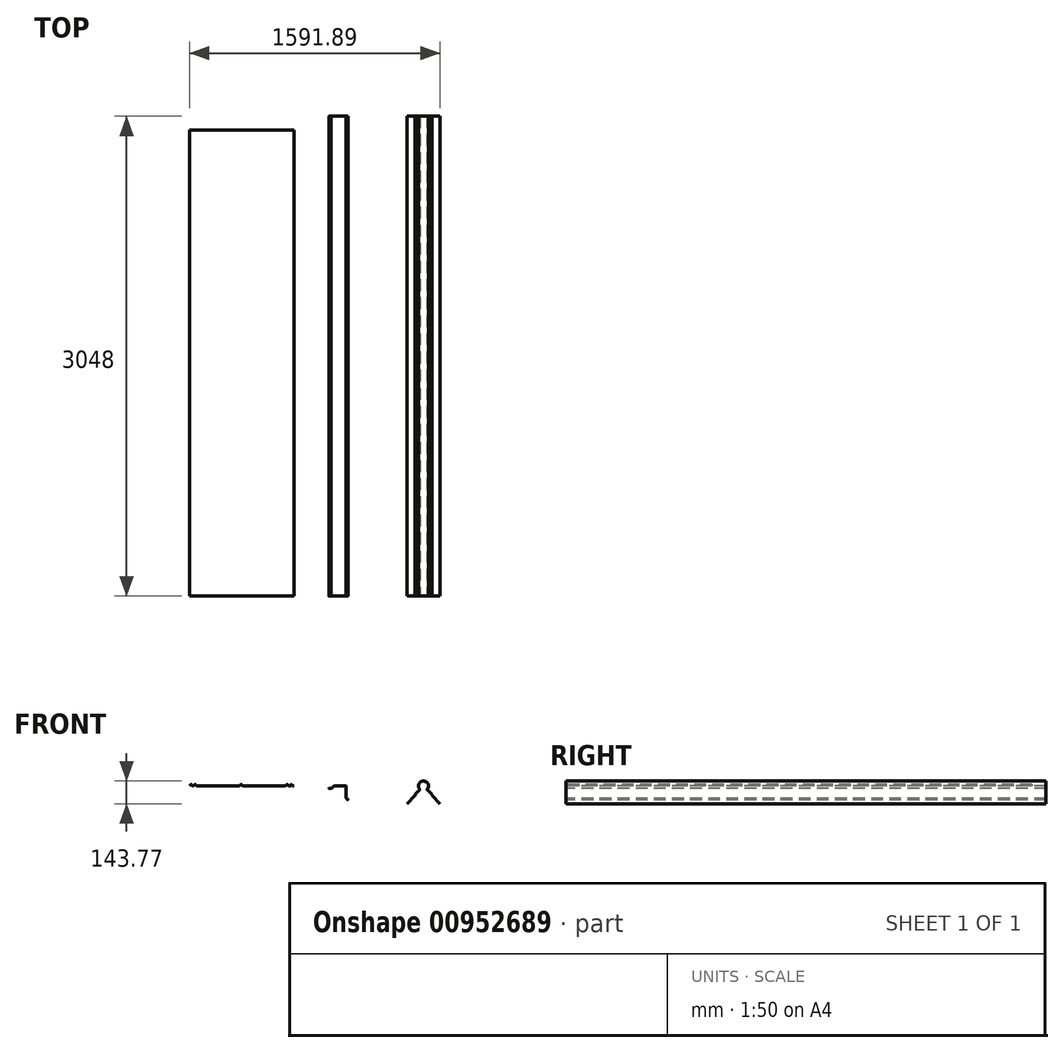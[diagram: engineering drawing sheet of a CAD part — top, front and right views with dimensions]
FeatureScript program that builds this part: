
annotation { "Feature Type Name" : "Feature", "Feature Type Description" : "" }
export const myFeature = defineFeature(function(context is Context, id is Id, definition is map)
    precondition{}
    {
        {
            var Q0;
            Q0=qCreatedBy(makeId("Front.planeOp"),FACE);
            var sketch = newSketch(context, id + "F0", { "sketchPlane" : qUnion([Q0])});
            skLineSegment(sketch, "E0.top", {"start": v(-1486.48, 424.6) * mm, "end": v(-822.9, 424.6) * mm, "construction": true});
            skLineSegment(sketch, "E0.left", {"start": v(-1486.48, 413.38) * mm, "end": v(-1486.48, 424.6) * mm, "construction": true});
            skLineSegment(sketch, "E0.right", {"start": v(-822.9, 413.38) * mm, "end": v(-822.9, 424.6) * mm, "construction": true});
            skLineSegment(sketch, "E1", {"start": v(-1485.6, 413.82) * mm, "end": v(-1475.55, 424.4) * mm});
            skLineSegment(sketch, "E2", {"start": v(-1475.55, 423.88) * mm, "end": v(-1485.44, 413.46) * mm});
            skLineSegment(sketch, "E3", {"start": v(-1475.18, 423.88) * mm, "end": v(-1465.29, 413.46) * mm});
            skLineSegment(sketch, "E4", {"start": v(-1475.18, 424.4) * mm, "end": v(-1465.14, 413.82) * mm});
            skPoint(sketch, "E5.visualSharp", {"position": v(-1475.37, 424.6) * mm});
            skArc(sketch, "E5.filletArc", {"start": v(-1475.18, 424.4) * mm, "mid": v(-1475.37, 424.48) * mm, "end": v(-1475.55, 424.4) * mm});
            skPoint(sketch, "E6.visualSharp", {"position": v(-1475.37, 424.08) * mm});
            skArc(sketch, "E6.filletArc", {"start": v(-1475.18, 423.88) * mm, "mid": v(-1475.37, 423.96) * mm, "end": v(-1475.55, 423.88) * mm});
            skPoint(sketch, "E7", {"position": v(-1475.37, 424.48) * mm});
            skPoint(sketch, "E8", {"position": v(-1465.21, 413.38) * mm});
            skPoint(sketch, "E9", {"position": v(-1485.52, 413.38) * mm});
            skPoint(sketch, "E10", {"position": v(-1465.06, 413.74) * mm});
            skPoint(sketch, "E11.1.0.0", {"position": v(-1449.97, 424.6) * mm});
            skPoint(sketch, "E11.1.0.1", {"position": v(-1449.97, 424.08) * mm});
            skPoint(sketch, "E11.1.0.2", {"position": v(-1460.27, 413.74) * mm});
            skPoint(sketch, "E11.1.0.3", {"position": v(-1460.12, 413.38) * mm});
            skPoint(sketch, "E11.1.0.4", {"position": v(-1439.66, 413.74) * mm});
            skPoint(sketch, "E11.1.0.5", {"position": v(-1439.81, 413.38) * mm});
            skPoint(sketch, "E12.1.0.0", {"position": v(-1157.87, 424.6) * mm});
            skPoint(sketch, "E12.1.0.1", {"position": v(-1157.87, 424.08) * mm});
            skPoint(sketch, "E12.1.0.2", {"position": v(-1168.17, 413.74) * mm});
            skPoint(sketch, "E12.1.0.3", {"position": v(-1168.02, 413.38) * mm});
            skPoint(sketch, "E12.1.0.4", {"position": v(-1147.71, 413.38) * mm});
            skPoint(sketch, "E12.1.0.5", {"position": v(-1147.56, 413.74) * mm});
            skPoint(sketch, "E12.2.0.0", {"position": v(-865.77, 424.6) * mm});
            skPoint(sketch, "E12.2.0.1", {"position": v(-865.77, 424.08) * mm});
            skPoint(sketch, "E12.2.0.2", {"position": v(-876.07, 413.74) * mm});
            skPoint(sketch, "E12.2.0.3", {"position": v(-875.92, 413.38) * mm});
            skPoint(sketch, "E12.2.0.4", {"position": v(-855.61, 413.38) * mm});
            skPoint(sketch, "E12.2.0.5", {"position": v(-855.46, 413.74) * mm});
            skLineSegment(sketch, "E12.direction1", {"start": v(-1449.97, 424.6) * mm, "end": v(-1157.87, 424.6) * mm, "construction": true});
            skPoint(sketch, "E13.1.0.0", {"position": v(-840.37, 424.6) * mm});
            skPoint(sketch, "E13.1.0.1", {"position": v(-830.06, 413.74) * mm});
            skPoint(sketch, "E13.1.0.2", {"position": v(-830.21, 413.38) * mm});
            skPoint(sketch, "E13.1.0.3", {"position": v(-840.26, 423.96) * mm});
            skLineSegment(sketch, "E13.direction1", {"start": v(-865.77, 424.6) * mm, "end": v(-840.37, 424.6) * mm, "construction": true});
            skPoint(sketch, "E14", {"position": v(-845.13, 413.74) * mm});
            skLineSegment(sketch, "E15", {"start": v(-1460.2, 413.82) * mm, "end": v(-1450.15, 424.4) * mm});
            skLineSegment(sketch, "E16", {"start": v(-1460.04, 413.46) * mm, "end": v(-1450.15, 423.88) * mm});
            skLineSegment(sketch, "E17", {"start": v(-1449.78, 424.4) * mm, "end": v(-1439.74, 413.82) * mm});
            skLineSegment(sketch, "E18", {"start": v(-1449.78, 423.88) * mm, "end": v(-1439.89, 413.46) * mm});
            skLineSegment(sketch, "E19", {"start": v(-1168.1, 413.82) * mm, "end": v(-1158.05, 424.4) * mm});
            skLineSegment(sketch, "E20", {"start": v(-1167.94, 413.46) * mm, "end": v(-1158.05, 423.88) * mm});
            skLineSegment(sketch, "E21", {"start": v(-1157.68, 424.4) * mm, "end": v(-1147.64, 413.82) * mm});
            skLineSegment(sketch, "E22", {"start": v(-1157.68, 423.88) * mm, "end": v(-1147.79, 413.46) * mm});
            skLineSegment(sketch, "E23", {"start": v(-876, 413.82) * mm, "end": v(-865.95, 424.4) * mm});
            skLineSegment(sketch, "E24", {"start": v(-865.58, 424.4) * mm, "end": v(-855.54, 413.82) * mm});
            skLineSegment(sketch, "E25", {"start": v(-875.84, 413.46) * mm, "end": v(-865.95, 423.88) * mm});
            skLineSegment(sketch, "E26", {"start": v(-865.58, 423.88) * mm, "end": v(-855.69, 413.46) * mm});
            skLineSegment(sketch, "E27", {"start": v(-845.06, 413.89) * mm, "end": v(-840.52, 424.25) * mm});
            skLineSegment(sketch, "E28", {"start": v(-840.4, 423.61) * mm, "end": v(-844.83, 413.53) * mm});
            skLineSegment(sketch, "E29", {"start": v(-840.1, 424.32) * mm, "end": v(-830.14, 413.82) * mm});
            skLineSegment(sketch, "E30", {"start": v(-840, 423.68) * mm, "end": v(-830.29, 413.46) * mm});
            skLineSegment(sketch, "E31", {"start": v(-1486.48, 413.38) * mm, "end": v(-1486.48, 413.74) * mm});
            skLineSegment(sketch, "E32", {"start": v(-1486.48, 413.74) * mm, "end": v(-1485.78, 413.74) * mm});
            skLineSegment(sketch, "E33", {"start": v(-1486.48, 413.38) * mm, "end": v(-1485.63, 413.38) * mm});
            skLineSegment(sketch, "E34", {"start": v(-830.1, 413.38) * mm, "end": v(-822.9, 413.38) * mm});
            skLineSegment(sketch, "E35", {"start": v(-822.9, 413.38) * mm, "end": v(-822.9, 413.74) * mm});
            skLineSegment(sketch, "E36", {"start": v(-822.9, 413.74) * mm, "end": v(-829.95, 413.74) * mm});
            skLineSegment(sketch, "E37", {"start": v(-845.3, 413.74) * mm, "end": v(-855.35, 413.74) * mm});
            skLineSegment(sketch, "E38", {"start": v(-855.5, 413.38) * mm, "end": v(-845.06, 413.38) * mm});
            skLineSegment(sketch, "E39", {"start": v(-876.18, 413.74) * mm, "end": v(-1147.45, 413.74) * mm});
            skLineSegment(sketch, "E40", {"start": v(-1147.6, 413.38) * mm, "end": v(-876.03, 413.38) * mm});
            skLineSegment(sketch, "E41", {"start": v(-1168.28, 413.74) * mm, "end": v(-1439.55, 413.74) * mm});
            skLineSegment(sketch, "E42", {"start": v(-1439.7, 413.38) * mm, "end": v(-1168.13, 413.38) * mm});
            skLineSegment(sketch, "E43", {"start": v(-1464.95, 413.74) * mm, "end": v(-1460.38, 413.74) * mm});
            skLineSegment(sketch, "E44", {"start": v(-1465.1, 413.38) * mm, "end": v(-1460.23, 413.38) * mm});
            skPoint(sketch, "E45.visualSharp", {"position": v(-1485.67, 413.74) * mm});
            skArc(sketch, "E45.filletArc", {"start": v(-1485.78, 413.74) * mm, "mid": v(-1485.68, 413.76) * mm, "end": v(-1485.6, 413.82) * mm});
            skArc(sketch, "E46.filletArc", {"start": v(-1485.63, 413.38) * mm, "mid": v(-1485.53, 413.4) * mm, "end": v(-1485.44, 413.46) * mm});
            skArc(sketch, "E47.filletArc", {"start": v(-1465.14, 413.82) * mm, "mid": v(-1465.05, 413.76) * mm, "end": v(-1464.95, 413.74) * mm});
            skArc(sketch, "E48.filletArc", {"start": v(-1465.29, 413.46) * mm, "mid": v(-1465.2, 413.4) * mm, "end": v(-1465.1, 413.38) * mm});
            skArc(sketch, "E49.filletArc", {"start": v(-1460.38, 413.74) * mm, "mid": v(-1460.28, 413.76) * mm, "end": v(-1460.2, 413.82) * mm});
            skArc(sketch, "E50.filletArc", {"start": v(-1460.23, 413.38) * mm, "mid": v(-1460.13, 413.4) * mm, "end": v(-1460.04, 413.46) * mm});
            skArc(sketch, "E51.filletArc", {"start": v(-1439.89, 413.46) * mm, "mid": v(-1439.8, 413.4) * mm, "end": v(-1439.7, 413.38) * mm});
            skArc(sketch, "E52.filletArc", {"start": v(-1439.74, 413.82) * mm, "mid": v(-1439.65, 413.76) * mm, "end": v(-1439.55, 413.74) * mm});
            skArc(sketch, "E53.filletArc", {"start": v(-1168.13, 413.38) * mm, "mid": v(-1168.03, 413.4) * mm, "end": v(-1167.94, 413.46) * mm});
            skArc(sketch, "E54.filletArc", {"start": v(-1168.28, 413.74) * mm, "mid": v(-1168.18, 413.76) * mm, "end": v(-1168.1, 413.82) * mm});
            skArc(sketch, "E55.filletArc", {"start": v(-1147.79, 413.46) * mm, "mid": v(-1147.7, 413.4) * mm, "end": v(-1147.6, 413.38) * mm});
            skArc(sketch, "E56.filletArc", {"start": v(-1147.64, 413.82) * mm, "mid": v(-1147.55, 413.76) * mm, "end": v(-1147.45, 413.74) * mm});
            skArc(sketch, "E57.filletArc", {"start": v(-876.18, 413.74) * mm, "mid": v(-876.08, 413.76) * mm, "end": v(-876, 413.82) * mm});
            skArc(sketch, "E58.filletArc", {"start": v(-876.03, 413.38) * mm, "mid": v(-875.93, 413.4) * mm, "end": v(-875.84, 413.46) * mm});
            skArc(sketch, "E59.filletArc", {"start": v(-865.58, 423.88) * mm, "mid": v(-865.77, 423.96) * mm, "end": v(-865.95, 423.88) * mm});
            skArc(sketch, "E60.filletArc", {"start": v(-865.58, 424.4) * mm, "mid": v(-865.77, 424.48) * mm, "end": v(-865.95, 424.4) * mm});
            skArc(sketch, "E61.filletArc", {"start": v(-855.54, 413.82) * mm, "mid": v(-855.45, 413.76) * mm, "end": v(-855.35, 413.74) * mm});
            skArc(sketch, "E62.filletArc", {"start": v(-855.69, 413.46) * mm, "mid": v(-855.6, 413.4) * mm, "end": v(-855.5, 413.38) * mm});
            skArc(sketch, "E63.filletArc", {"start": v(-845.3, 413.74) * mm, "mid": v(-845.16, 413.78) * mm, "end": v(-845.06, 413.89) * mm});
            skPoint(sketch, "E64.visualSharp", {"position": v(-844.9, 413.38) * mm});
            skArc(sketch, "E64.filletArc", {"start": v(-845.06, 413.38) * mm, "mid": v(-844.92, 413.42) * mm, "end": v(-844.83, 413.53) * mm});
            skArc(sketch, "E65.filletArc", {"start": v(-840.1, 424.32) * mm, "mid": v(-840.33, 424.4) * mm, "end": v(-840.52, 424.25) * mm});
            skArc(sketch, "E66.filletArc", {"start": v(-840, 423.68) * mm, "mid": v(-840.22, 423.76) * mm, "end": v(-840.4, 423.61) * mm});
            skArc(sketch, "E67.filletArc", {"start": v(-830.14, 413.82) * mm, "mid": v(-830.05, 413.76) * mm, "end": v(-829.95, 413.74) * mm});
            skArc(sketch, "E68.filletArc", {"start": v(-830.29, 413.46) * mm, "mid": v(-830.2, 413.4) * mm, "end": v(-830.1, 413.38) * mm});
            skArc(sketch, "E69.filletArc", {"start": v(-1157.68, 423.88) * mm, "mid": v(-1157.87, 423.96) * mm, "end": v(-1158.05, 423.88) * mm});
            skArc(sketch, "E70.filletArc", {"start": v(-1157.68, 424.4) * mm, "mid": v(-1157.87, 424.48) * mm, "end": v(-1158.05, 424.4) * mm});
            skArc(sketch, "E71.filletArc", {"start": v(-1449.78, 423.88) * mm, "mid": v(-1449.97, 423.96) * mm, "end": v(-1450.15, 423.88) * mm});
            skArc(sketch, "E72.filletArc", {"start": v(-1449.78, 424.4) * mm, "mid": v(-1449.97, 424.48) * mm, "end": v(-1450.15, 424.4) * mm});
            skArc(sketch, "E73", {"start": v(22.63, 391.1) * mm, "mid": v(0, 445.13) * mm, "end": v(-22.63, 391.1) * mm});
            skArc(sketch, "E74", {"start": v(22.13, 391.1) * mm, "mid": v(0, 444.77) * mm, "end": v(-22.13, 391.1) * mm});
            skLineSegment(sketch, "E75", {"start": v(0, 413.38) * mm, "end": v(0.25, 413.13) * mm});
            skLineSegment(sketch, "E76", {"start": v(0, 413.38) * mm, "end": v(0, 231.35) * mm, "construction": true});
            skCircle(sketch, "E77", {"center": v(0, 413.38) * mm, "radius": 0.36 * mm, "construction": true});
            skLineSegment(sketch, "E78", {"start": v(0.25, 413.13) * mm, "end": v(0, 412.87) * mm, "construction": true});
            skLineSegment(sketch, "E79", {"start": v(0, 412.87) * mm, "end": v(-0.25, 413.13) * mm, "construction": true});
            skLineSegment(sketch, "E80", {"start": v(22.12, 390.75) * mm, "end": v(53.45, 359.42) * mm});
            skLineSegment(sketch, "E81", {"start": v(53.52, 359.24) * mm, "end": v(53.52, 353.1) * mm});
            skLineSegment(sketch, "E82.1.0.0", {"start": v(53.88, 359.4) * mm, "end": v(53.88, 353.25) * mm});
            skLineSegment(sketch, "E83", {"start": v(53.6, 352.93) * mm, "end": v(105.16, 301.36) * mm});
            skLineSegment(sketch, "E84.trimOffspring", {"start": v(22.63, 390.75) * mm, "end": v(53.8, 359.57) * mm});
            skLineSegment(sketch, "E85", {"start": v(105.16, 301.36) * mm, "end": v(105.41, 301.62) * mm});
            skLineSegment(sketch, "E86", {"start": v(105.41, 301.62) * mm, "end": v(53.96, 353.07) * mm});
            skPoint(sketch, "E87.visualSharp", {"position": v(21.94, 390.93) * mm});
            skArc(sketch, "E87.filletArc", {"start": v(22.13, 391.1) * mm, "mid": v(22.05, 390.93) * mm, "end": v(22.12, 390.75) * mm});
            skPoint(sketch, "E88.visualSharp", {"position": v(22.45, 390.93) * mm});
            skArc(sketch, "E88.filletArc", {"start": v(22.63, 391.1) * mm, "mid": v(22.56, 390.93) * mm, "end": v(22.63, 390.75) * mm});
            skPoint(sketch, "E89.visualSharp", {"position": v(53.52, 359.35) * mm});
            skArc(sketch, "E89.filletArc", {"start": v(53.52, 359.24) * mm, "mid": v(53.5, 359.34) * mm, "end": v(53.45, 359.42) * mm});
            skPoint(sketch, "E90.visualSharp", {"position": v(53.88, 359.5) * mm});
            skArc(sketch, "E90.filletArc", {"start": v(53.88, 359.4) * mm, "mid": v(53.86, 359.5) * mm, "end": v(53.8, 359.57) * mm});
            skPoint(sketch, "E91.visualSharp", {"position": v(53.52, 353) * mm});
            skArc(sketch, "E91.filletArc", {"start": v(53.52, 353.1) * mm, "mid": v(53.54, 353) * mm, "end": v(53.6, 352.93) * mm});
            skPoint(sketch, "E92.visualSharp", {"position": v(53.88, 353.15) * mm});
            skArc(sketch, "E92.filletArc", {"start": v(53.88, 353.25) * mm, "mid": v(53.9, 353.16) * mm, "end": v(53.96, 353.07) * mm});
            skArc(sketch, "E93.MirrorCS", {"start": v(-22.13, 391.1) * mm, "mid": v(-22.05, 390.93) * mm, "end": v(-22.12, 390.75) * mm});
            skArc(sketch, "E94.MirrorCS", {"start": v(-22.63, 391.1) * mm, "mid": v(-22.56, 390.93) * mm, "end": v(-22.63, 390.75) * mm});
            skPoint(sketch, "E95.MirrorP", {"position": v(-21.94, 390.93) * mm});
            skPoint(sketch, "E96.MirrorP", {"position": v(-22.45, 390.93) * mm});
            skLineSegment(sketch, "E97.MirrorCS", {"start": v(-22.12, 390.75) * mm, "end": v(-53.45, 359.42) * mm});
            skLineSegment(sketch, "E98.MirrorCS", {"start": v(-22.63, 390.75) * mm, "end": v(-53.8, 359.57) * mm});
            skArc(sketch, "E99.MirrorCS", {"start": v(-53.52, 353.1) * mm, "mid": v(-53.54, 353) * mm, "end": v(-53.6, 352.93) * mm});
            skArc(sketch, "E100.MirrorCS", {"start": v(-53.52, 359.24) * mm, "mid": v(-53.5, 359.34) * mm, "end": v(-53.45, 359.42) * mm});
            skArc(sketch, "E101.MirrorCS", {"start": v(-53.88, 353.25) * mm, "mid": v(-53.9, 353.16) * mm, "end": v(-53.96, 353.07) * mm});
            skArc(sketch, "E102.MirrorCS", {"start": v(-53.88, 359.4) * mm, "mid": v(-53.86, 359.5) * mm, "end": v(-53.8, 359.57) * mm});
            skLineSegment(sketch, "E103.MirrorCS", {"start": v(-53.52, 359.24) * mm, "end": v(-53.52, 353.1) * mm});
            skLineSegment(sketch, "E104.MirrorCS", {"start": v(-53.88, 359.4) * mm, "end": v(-53.88, 353.25) * mm});
            skLineSegment(sketch, "E105.MirrorCS", {"start": v(-105.16, 301.36) * mm, "end": v(-105.41, 301.62) * mm});
            skPoint(sketch, "E106.MirrorP", {"position": v(-53.88, 353.15) * mm});
            skPoint(sketch, "E107.MirrorP", {"position": v(-53.52, 359.35) * mm});
            skPoint(sketch, "E108.MirrorP", {"position": v(-53.88, 359.5) * mm});
            skPoint(sketch, "E109.MirrorP", {"position": v(-53.52, 353) * mm});
            skLineSegment(sketch, "E110.MirrorCS", {"start": v(-53.6, 352.93) * mm, "end": v(-105.16, 301.36) * mm});
            skLineSegment(sketch, "E111.MirrorCS", {"start": v(-105.41, 301.62) * mm, "end": v(-53.96, 353.07) * mm});
            skLineSegment(sketch, "E112.left", {"start": v(-822.9, 413.38) * mm, "end": v(-822.9, 413.74) * mm, "construction": true});
            skLineSegment(sketch, "E113", {"start": v(-568.6, 413.74) * mm, "end": v(-491.83, 413.74) * mm});
            skLineSegment(sketch, "E114", {"start": v(-568.6, 413.38) * mm, "end": v(-491.83, 413.38) * mm});
            skLineSegment(sketch, "E115", {"start": v(-491.12, 413.02) * mm, "end": v(-491.12, 337.83) * mm});
            skLineSegment(sketch, "E116", {"start": v(-491.01, 337.58) * mm, "end": v(-480.74, 327.31) * mm});
            skLineSegment(sketch, "E117", {"start": v(-482.27, 325.9) * mm, "end": v(-489.62, 334.68) * mm});
            skLineSegment(sketch, "E118", {"start": v(-489.35, 334.9) * mm, "end": v(-482, 326.14) * mm});
            skLineSegment(sketch, "E119", {"start": v(-481, 327.06) * mm, "end": v(-491.26, 337.33) * mm});
            skLineSegment(sketch, "E120", {"start": v(-491.47, 337.83) * mm, "end": v(-491.47, 413.02) * mm});
            skPoint(sketch, "E121.visualSharp", {"position": v(-491.47, 337.54) * mm});
            skArc(sketch, "E121.filletArc", {"start": v(-491.47, 337.83) * mm, "mid": v(-491.42, 337.56) * mm, "end": v(-491.26, 337.33) * mm});
            skArc(sketch, "E122.filletArc", {"start": v(-491.12, 413.02) * mm, "mid": v(-491.33, 413.53) * mm, "end": v(-491.83, 413.74) * mm});
            skPoint(sketch, "E123.visualSharp", {"position": v(-490.97, 337.54) * mm});
            skLineSegment(sketch, "E124", {"start": v(-584.77, 397.66) * mm, "end": v(-599.27, 397.66) * mm});
            skLineSegment(sketch, "E125", {"start": v(-625.98, 383.07) * mm, "end": v(-625.98, 383.07) * mm});
            skLineSegment(sketch, "E126", {"start": v(-587.77, 398.38) * mm, "end": v(-599.2, 399.39) * mm});
            skLineSegment(sketch, "E127", {"start": v(-599.27, 398.02) * mm, "end": v(-584.77, 398.02) * mm});
            skLineSegment(sketch, "E128", {"start": v(-569.11, 413.53) * mm, "end": v(-584.51, 398.13) * mm});
            skLineSegment(sketch, "E129", {"start": v(-568.86, 413.27) * mm, "end": v(-584.26, 397.87) * mm});
            skLineSegment(sketch, "E130", {"start": v(-587.74, 398.73) * mm, "end": v(-599.18, 399.74) * mm});
            skArc(sketch, "E131", {"start": v(-599.18, 399.74) * mm, "mid": v(-600.3, 398.75) * mm, "end": v(-599.27, 397.66) * mm, "construction": true});
            skArc(sketch, "E132", {"start": v(-599.2, 399.39) * mm, "mid": v(-599.95, 398.73) * mm, "end": v(-599.27, 398.02) * mm});
            skArc(sketch, "E133", {"start": v(-599.18, 399.74) * mm, "mid": v(-600.3, 398.75) * mm, "end": v(-599.27, 397.66) * mm});
            skPoint(sketch, "E134", {"position": v(-600.3, 398.75) * mm});
            skArc(sketch, "E135", {"start": v(-587.74, 398.73) * mm, "mid": v(-587.58, 398.54) * mm, "end": v(-587.77, 398.38) * mm});
            skPoint(sketch, "E136", {"position": v(-587.58, 398.54) * mm});
            skLineSegment(sketch, "E137", {"start": v(-600.3, 398.75) * mm, "end": v(-600.23, 399.65) * mm, "construction": true});
            skLineSegment(sketch, "E138", {"start": v(-600.23, 399.65) * mm, "end": v(-587.58, 398.54) * mm, "construction": true});
            skPoint(sketch, "E139.visualSharp", {"position": v(-584.62, 398.02) * mm});
            skArc(sketch, "E139.filletArc", {"start": v(-584.77, 398.02) * mm, "mid": v(-584.63, 398.05) * mm, "end": v(-584.51, 398.13) * mm});
            skArc(sketch, "E140.filletArc", {"start": v(-568.6, 413.38) * mm, "mid": v(-568.74, 413.35) * mm, "end": v(-568.86, 413.27) * mm});
            skArc(sketch, "E141.filletArc", {"start": v(-491.47, 413.02) * mm, "mid": v(-491.58, 413.27) * mm, "end": v(-491.83, 413.38) * mm});
            skArc(sketch, "E142.filletArc", {"start": v(-491.12, 337.83) * mm, "mid": v(-491.09, 337.7) * mm, "end": v(-491.01, 337.58) * mm});
            skPoint(sketch, "E143.visualSharp", {"position": v(-568.9, 413.74) * mm});
            skArc(sketch, "E143.filletArc", {"start": v(-568.6, 413.74) * mm, "mid": v(-568.88, 413.68) * mm, "end": v(-569.11, 413.53) * mm});
            skPoint(sketch, "E144.visualSharp", {"position": v(-584.47, 397.66) * mm});
            skArc(sketch, "E144.filletArc", {"start": v(-584.77, 397.66) * mm, "mid": v(-584.5, 397.72) * mm, "end": v(-584.26, 397.87) * mm});
            skArc(sketch, "E145", {"start": v(-489.35, 334.9) * mm, "mid": v(-489.6, 334.93) * mm, "end": v(-489.62, 334.68) * mm});
            skArc(sketch, "E146", {"start": v(-482.27, 325.9) * mm, "mid": v(-480.77, 325.8) * mm, "end": v(-480.74, 327.31) * mm});
            skArc(sketch, "E147", {"start": v(-481, 327.06) * mm, "mid": v(-481.02, 326.07) * mm, "end": v(-482, 326.14) * mm});
            skPoint(sketch, "E148", {"position": v(-489.6, 334.93) * mm});
            skPoint(sketch, "E149", {"position": v(-480.77, 325.8) * mm});
            skPoint(sketch, "E150", {"position": v(-481.02, 326.07) * mm});
            skLineSegment(sketch, "E151", {"start": v(-489.6, 334.93) * mm, "end": v(-481.44, 325.2) * mm, "construction": true});
            skLineSegment(sketch, "E152", {"start": v(-480.77, 325.8) * mm, "end": v(-481.44, 325.2) * mm, "construction": true});
            skSolve(sketch);
        }
        {
            var Q0;
            Q0=makeQuery(id+"F0.imprint","IMPRINT",FACE,{"disambiguationData":[TD([[makeQuery(id+"F0.imprint","IMPRINT",EDGE,{"derivedFrom":sQuery(id+"F0.wireOp",EDGE,"E1")}),-1.0]])]});
            extrude(context, id + "F1", {"entities" : qUnion([Q0]), "oppositeDirection" : true, "depth" : 2959.1 * mm, "offsetDistance" : 25.4 * mm});
        }
        {
            var Q0;
            Q0=makeQuery(id+"F0.imprint","IMPRINT",FACE,{"disambiguationData":[TD([[makeQuery(id+"F0.imprint","IMPRINT",EDGE,{"derivedFrom":sQuery(id+"F0.wireOp",EDGE,"E73")}),1.0]])]});
            extrude(context, id + "F2", {"entities" : qUnion([Q0]), "oppositeDirection" : true, "depth" : 3048 * mm, "offsetDistance" : 25.4 * mm});
        }
        {
            var Q0;
            Q0=makeQuery(id+"F0.imprint","IMPRINT",FACE,{"disambiguationData":[TD([[makeQuery(id+"F0.imprint","IMPRINT",EDGE,{"derivedFrom":sQuery(id+"F0.wireOp",EDGE,"E113")}),-1.0]])]});
            extrude(context, id + "F3", {"entities" : qUnion([Q0]), "oppositeDirection" : true, "depth" : 3048 * mm, "offsetDistance" : 25.4 * mm});
        }
    });
